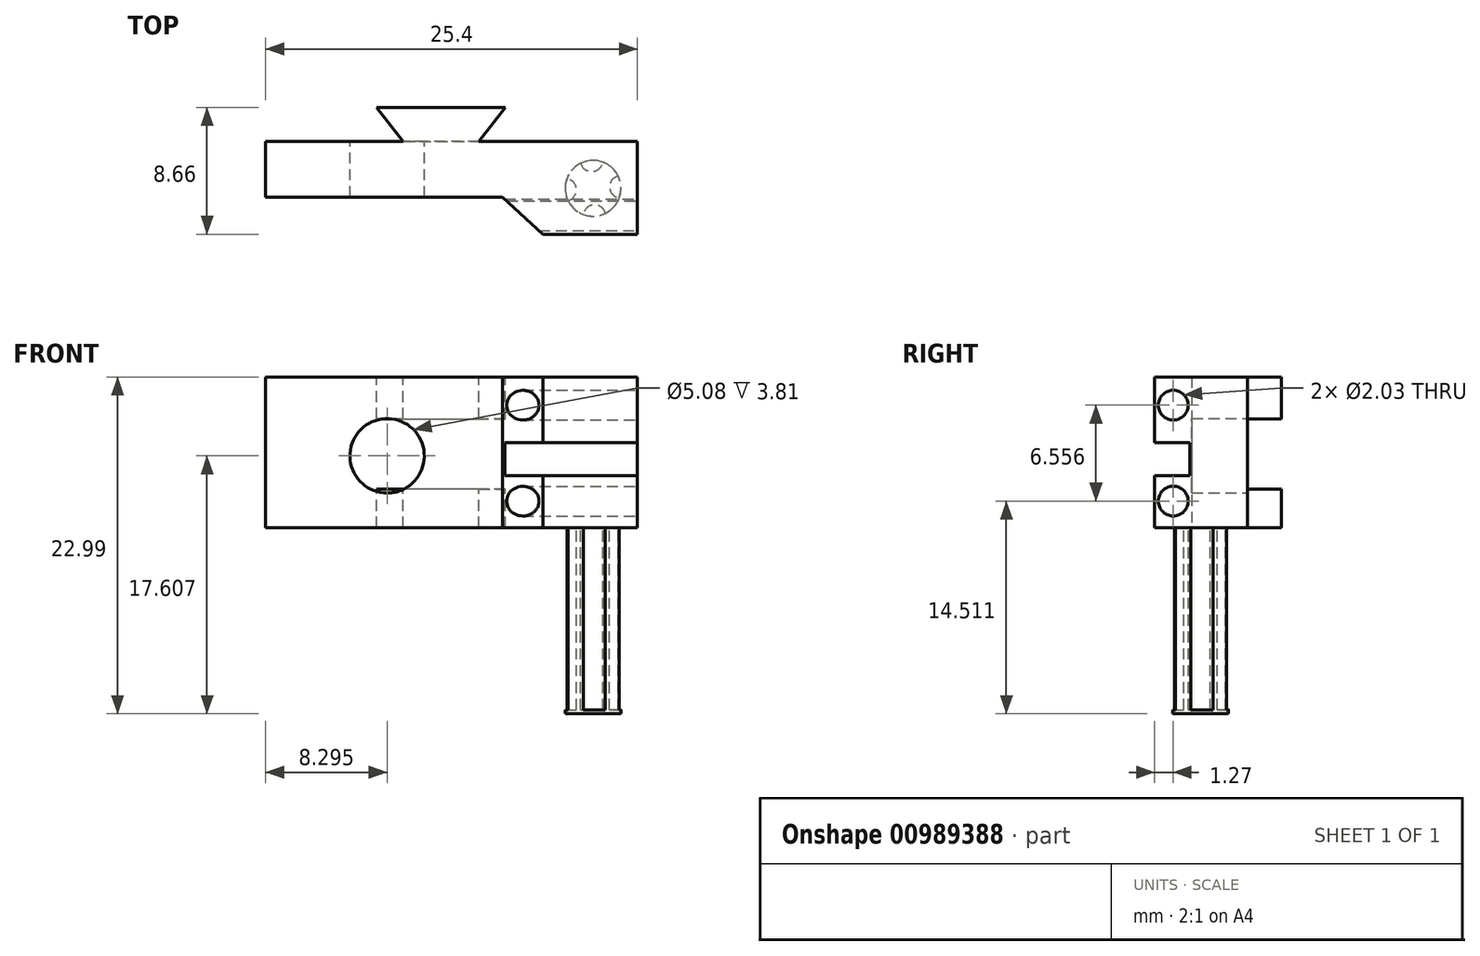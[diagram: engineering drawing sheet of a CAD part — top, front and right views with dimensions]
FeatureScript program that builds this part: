
annotation { "Feature Type Name" : "Feature", "Feature Type Description" : "" }
export const myFeature = defineFeature(function(context is Context, id is Id, definition is map)
    precondition{}
    {
        {
            var Q0;
            Q0=qCreatedBy(makeId("Front.planeOp"),FACE);
            var sketch = newSketch(context, id + "F0", { "sketchPlane" : qUnion([Q0])});
            skLineSegment(sketch, "E0.bottom", {"start": v(-61.12, 37.28) * mm, "end": v(-35.72, 37.28) * mm});
            skLineSegment(sketch, "E0.top", {"start": v(-61.12, 27) * mm, "end": v(-35.72, 27) * mm});
            skLineSegment(sketch, "E0.left", {"start": v(-61.12, 37.28) * mm, "end": v(-61.12, 27) * mm});
            skLineSegment(sketch, "E0.right", {"start": v(-35.72, 37.28) * mm, "end": v(-35.72, 27) * mm});
            skCircle(sketch, "E1", {"center": v(-52.82, 31.9) * mm, "radius": 2.54 * mm});
            skSolve(sketch);
        }
        {
            var Q0;
            Q0 = qSketchRegion(id + "F0", true);
            extrude(context, id + "F1", {"entities" : qUnion([Q0]), "depth" : 6.35 * mm, "offsetDistance" : 25.4 * mm});
        }
        {
            var Q0;
            Q0=makeQuery(id+"F1.opExtrude","SWEPT_FACE",FACE,{"disambiguationData":[OSD([sQuery(id+"F0.wireOp",EDGE,"E0.right")])]});
            var sketch = newSketch(context, id + "F2", { "sketchPlane" : qUnion([Q0])});
            skLineSegment(sketch, "E2", {"start": v(-6.35, 30.55) * mm, "end": v(-3.94, 30.55) * mm});
            skLineSegment(sketch, "E3", {"start": v(-3.94, 30.55) * mm, "end": v(-3.94, 32.79) * mm});
            skLineSegment(sketch, "E4", {"start": v(-3.94, 32.79) * mm, "end": v(-6.35, 32.79) * mm});
            skCircle(sketch, "E5", {"center": v(-5.08, 28.8) * mm, "radius": 1.02 * mm});
            skCircle(sketch, "E6", {"center": v(-5.08, 35.36) * mm, "radius": 1.02 * mm});
            skSolve(sketch);
        }
        {
            var Q0;
            Q0 = qSketchRegion(id + "F2", true);
            var Q1;
            {var subQ0=sQuery(id+"F2.wireOp",EDGE,"E2");Q1=makeQuery(id+"F2.imprint","IMPRINT",FACE,{"disambiguationData":[TD([[makeQuery(id+"F2.imprint","IMPRINT",EDGE,{"derivedFrom":subQ0}),1.0]])]});}
            extrude(context, id + "F3", {"entities" : qUnion([Q0, Q1]), "operationType" : NewBodyOperationType.REMOVE, "oppositeDirection" : true, "depth" : 25.4 * mm, "offsetDistance" : 25.4 * mm});
        }
        {
            var Q0;
            Q0=makeQuery(id+"F1.opExtrude","SWEPT_FACE",FACE,{"disambiguationData":[OSD([sQuery(id+"F0.wireOp",EDGE,"E0.top")])]});
            var sketch = newSketch(context, id + "F4", { "sketchPlane" : qUnion([Q0])});
            skLineSegment(sketch, "E7", {"start": v(-42.17, 6.35) * mm, "end": v(-44.93, 3.8) * mm});
            skLineSegment(sketch, "E8", {"start": v(-44.93, 3.81) * mm, "end": v(-61.12, 3.81) * mm});
            skSolve(sketch);
        }
        {
            var Q0;
            {var subQ0=sQuery(id+"F4.wireOp",EDGE,"E7");Q0=makeQuery(id+"F4.imprint","IMPRINT",FACE,{"disambiguationData":[TD([[makeQuery(id+"F4.imprint","IMPRINT",EDGE,{"derivedFrom":subQ0}),-1.0]])]});}
            extrude(context, id + "F5", {"entities" : qUnion([Q0]), "operationType" : NewBodyOperationType.REMOVE, "oppositeDirection" : true, "depth" : 25.4 * mm, "offsetDistance" : 25.4 * mm});
        }
        {
            var Q0;
            Q0=makeQuery(id+"F1.opExtrude","SWEPT_FACE",FACE,{"disambiguationData":[OSD([sQuery(id+"F0.wireOp",EDGE,"E0.top")])]});
            var sketch = newSketch(context, id + "F6", { "sketchPlane" : qUnion([Q0])});
            skCircle(sketch, "E9", {"center": v(-38.76, 3.2) * mm, "radius": 1.9 * mm});
            skSolve(sketch);
        }
        {
            var Q0;
            Q0 = qSketchRegion(id + "F6", true);
            extrude(context, id + "F7", {"entities" : qUnion([Q0]), "operationType" : NewBodyOperationType.ADD, "depth" : 12.7 * mm, "offsetDistance" : 25.4 * mm});
        }
        {
            var Q0;
            Q0=makeQuery(id+"F1.opExtrude","SWEPT_FACE",FACE,{"disambiguationData":[OSD([sQuery(id+"F0.wireOp",EDGE,"E0.top")])]});
            var sketch = newSketch(context, id + "F8", { "sketchPlane" : qUnion([Q0])});
            skCircle(sketch, "E10", {"center": v(-38.66, 5.11) * mm, "radius": 0.77 * mm});
            skCircle(sketch, "E11.1.0", {"center": v(-40.66, 3.3) * mm, "radius": 0.77 * mm});
            skCircle(sketch, "E11.2.0", {"center": v(-38.85, 1.3) * mm, "radius": 0.77 * mm});
            skCircle(sketch, "E11.3.0", {"center": v(-36.85, 3.11) * mm, "radius": 0.77 * mm});
            skPoint(sketch, "E11.center", {"position": v(-38.76, 3.2) * mm});
            skSolve(sketch);
        }
        {
            var Q0;
            Q0 = qSketchRegion(id + "F8", true);
            extrude(context, id + "F9", {"entities" : qUnion([Q0]), "operationType" : NewBodyOperationType.REMOVE, "depth" : 12.45 * mm, "offsetDistance" : 25.4 * mm});
        }
        {
            var Q0;
            Q0=makeQuery(id+"F1.opExtrude","SWEPT_FACE",FACE,{"disambiguationData":[OSD([sQuery(id+"F0.wireOp",EDGE,"E0.bottom")])]});
            var sketch = newSketch(context, id + "F10", { "sketchPlane" : qUnion([Q0])});
            skLineSegment(sketch, "E12", {"start": v(-46.55, 0) * mm, "end": v(-44.76, 2.3) * mm});
            skLineSegment(sketch, "E13", {"start": v(-44.76, 2.3) * mm, "end": v(-53.53, 2.3) * mm});
            skLineSegment(sketch, "E14", {"start": v(-53.53, 2.3) * mm, "end": v(-51.74, 0) * mm});
            skLineSegment(sketch, "E15", {"start": v(-51.74, 0) * mm, "end": v(-46.55, 0) * mm});
            skSolve(sketch);
        }
        {
            var Q0;
            Q0=makeQuery(id+"F10.imprint","IMPRINT",FACE,{"disambiguationData":[TD([[makeQuery(id+"F10.imprint","IMPRINT",EDGE,{"derivedFrom":sQuery(id+"F10.wireOp",EDGE,"E12")}),1.0]])]});
            extrude(context, id + "F11", {"entities" : qUnion([Q0]), "operationType" : NewBodyOperationType.ADD, "depth" : -10.29 * mm, "offsetDistance" : 25.4 * mm});
        }
        {
            var Q0;
            Q0=makeQuery(id+"F11.opExtrude","SWEPT_FACE",FACE,{"disambiguationData":[OSD([sQuery(id+"F10.wireOp",EDGE,"E13")])]});
            var sketch = newSketch(context, id + "F12", { "sketchPlane" : qUnion([Q0])});
            skLineSegment(sketch, "E16", {"start": v(53.53, 34.42) * mm, "end": v(44.76, 34.42) * mm});
            skLineSegment(sketch, "E17", {"start": v(44.76, 34.42) * mm, "end": v(44.76, 29.63) * mm});
            skLineSegment(sketch, "E18", {"start": v(44.76, 29.63) * mm, "end": v(53.53, 29.63) * mm});
            skSolve(sketch);
        }
        {
            var Q0;
            {var subQ0=sQuery(id+"F12.wireOp",EDGE,"E16");Q0=makeQuery(id+"F12.imprint","IMPRINT",FACE,{"disambiguationData":[TD([[makeQuery(id+"F12.imprint","IMPRINT",EDGE,{"derivedFrom":subQ0}),1.0]])]});}
            extrude(context, id + "F13", {"entities" : qUnion([Q0]), "operationType" : NewBodyOperationType.REMOVE, "oppositeDirection" : true, "depth" : 2.3 * mm, "offsetDistance" : 25.4 * mm});
        }
    });
